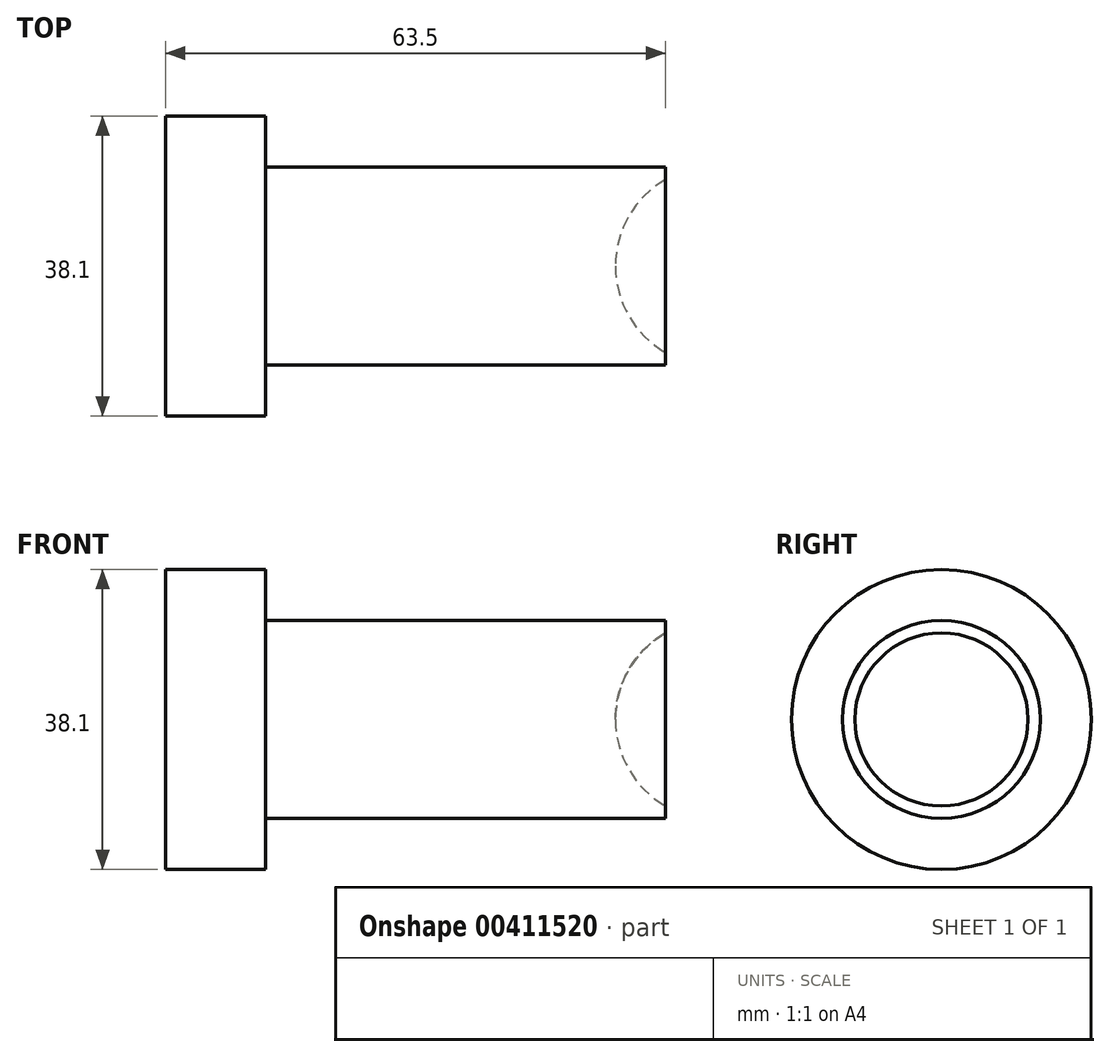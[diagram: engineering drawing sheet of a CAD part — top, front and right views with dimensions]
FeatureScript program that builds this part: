
annotation { "Feature Type Name" : "Feature", "Feature Type Description" : "" }
export const myFeature = defineFeature(function(context is Context, id is Id, definition is map)
    precondition{}
    {
        {
            var Q0;
            Q0=qCreatedBy(makeId("Front.planeOp"),FACE);
            var sketch = newSketch(context, id + "F0", { "sketchPlane" : qUnion([Q0])});
            skLineSegment(sketch, "E0", {"start": v(0, 0) * mm, "end": v(0, 19.05) * mm});
            skLineSegment(sketch, "E1", {"start": v(0, 19.05) * mm, "end": v(12.7, 19.05) * mm});
            skLineSegment(sketch, "E2", {"start": v(12.7, 19.05) * mm, "end": v(12.7, 12.57) * mm});
            skLineSegment(sketch, "E3", {"start": v(12.7, 12.57) * mm, "end": v(63.5, 12.57) * mm});
            skLineSegment(sketch, "E4", {"start": v(63.5, 12.57) * mm, "end": v(63.5, 11) * mm});
            skLineSegment(sketch, "E5", {"start": v(57.15, 0) * mm, "end": v(0, 0) * mm});
            skLineSegment(sketch, "E6", {"start": v(69.85, 21.9) * mm, "end": v(69.85, -8.25) * mm});
            skArc(sketch, "E7", {"start": v(63.5, 11) * mm, "mid": v(58.85, 6.35) * mm, "end": v(57.15, 0) * mm});
            skPoint(sketch, "E8.orphan", {"position": v(63.5, 0) * mm});
            skSolve(sketch);
        }
        {
            var Q0;
            Q0=makeQuery(id+"F0.imprint","IMPRINT",FACE,{"disambiguationData":[TD([[makeQuery(id+"F0.imprint","IMPRINT",EDGE,{"derivedFrom":sQuery(id+"F0.wireOp",EDGE,"E0")}),-1.0]])]});
            var Q1;
            Q1=sQuery(id+"F0.wireOp",EDGE,"E5");
            revolve(context, id + "F1", {"entities" : qUnion([Q0]), "axis" : qUnion([Q1]), "revolveType" : RevolveType.FULL});
        }
    });
